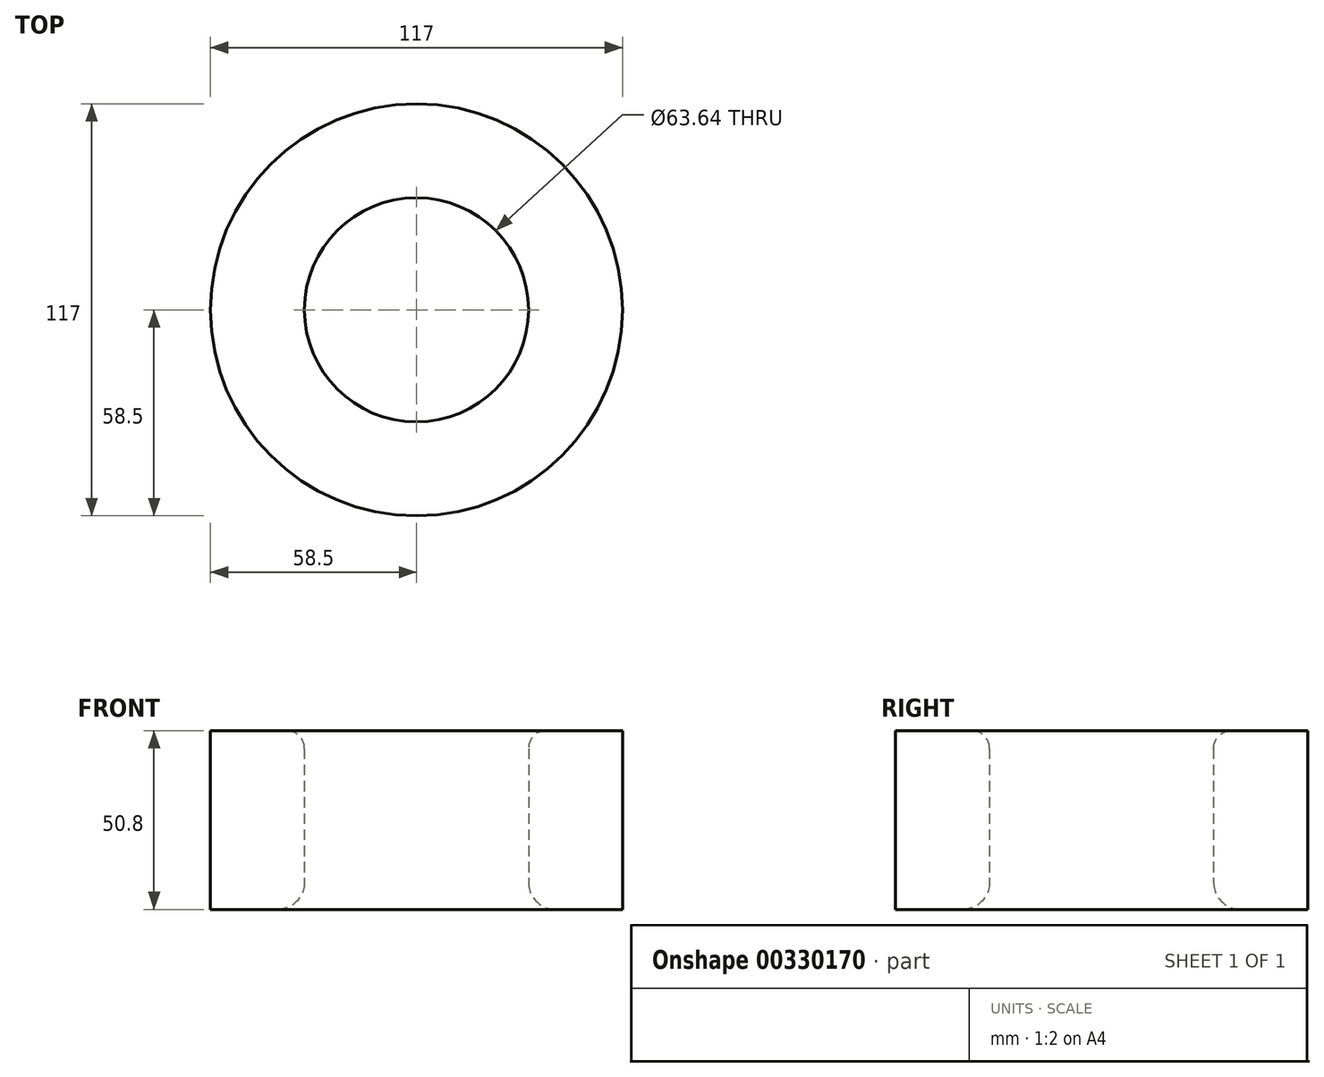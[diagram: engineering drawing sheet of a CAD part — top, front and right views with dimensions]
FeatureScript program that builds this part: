
annotation { "Feature Type Name" : "Feature", "Feature Type Description" : "" }
export const myFeature = defineFeature(function(context is Context, id is Id, definition is map)
    precondition{}
    {
        {
            var Q0;
            Q0=qCreatedBy(makeId("Top.planeOp"),FACE);
            var sketch = newSketch(context, id + "F0", { "sketchPlane" : qUnion([Q0])});
            skPoint(sketch, "E0", {"position": v(0, 0) * mm});
            skCircle(sketch, "E1", {"center": v(0, 0) * mm, "radius": 31.82 * mm});
            skCircle(sketch, "E2", {"center": v(0, 0) * mm, "radius": 58.5 * mm});
            skSolve(sketch);
        }
        {
            var Q0;
            Q0 = qSketchRegion(id + "F0", true);
            extrude(context, id + "F1", {"entities" : qUnion([Q0]), "depth" : 50.8 * mm});
        }
        {
            var Q0;
            Q0=makeQuery(id+"F1.opExtrude","CAP_EDGE",EDGE,{"disambiguationData":[OSD([sQuery(id+"F0.wireOp",EDGE,"E1")])],"isStart":false});
            fillet(context, id + "F2", {"entities" : qUnion([Q0]), "radius" : 5.08 * mm, "tangentPropagation" : true, "allowEdgeOverflow" : false});
        }
        {
            var Q0;
            Q0=makeQuery(id+"F1.opExtrude","CAP_EDGE",EDGE,{"disambiguationData":[OSD([sQuery(id+"F0.wireOp",EDGE,"E1")])],"isStart":true});
            fillet(context, id + "F3", {"entities" : qUnion([Q0]), "radius" : 7.62 * mm, "tangentPropagation" : true, "allowEdgeOverflow" : false});
        }
    });
